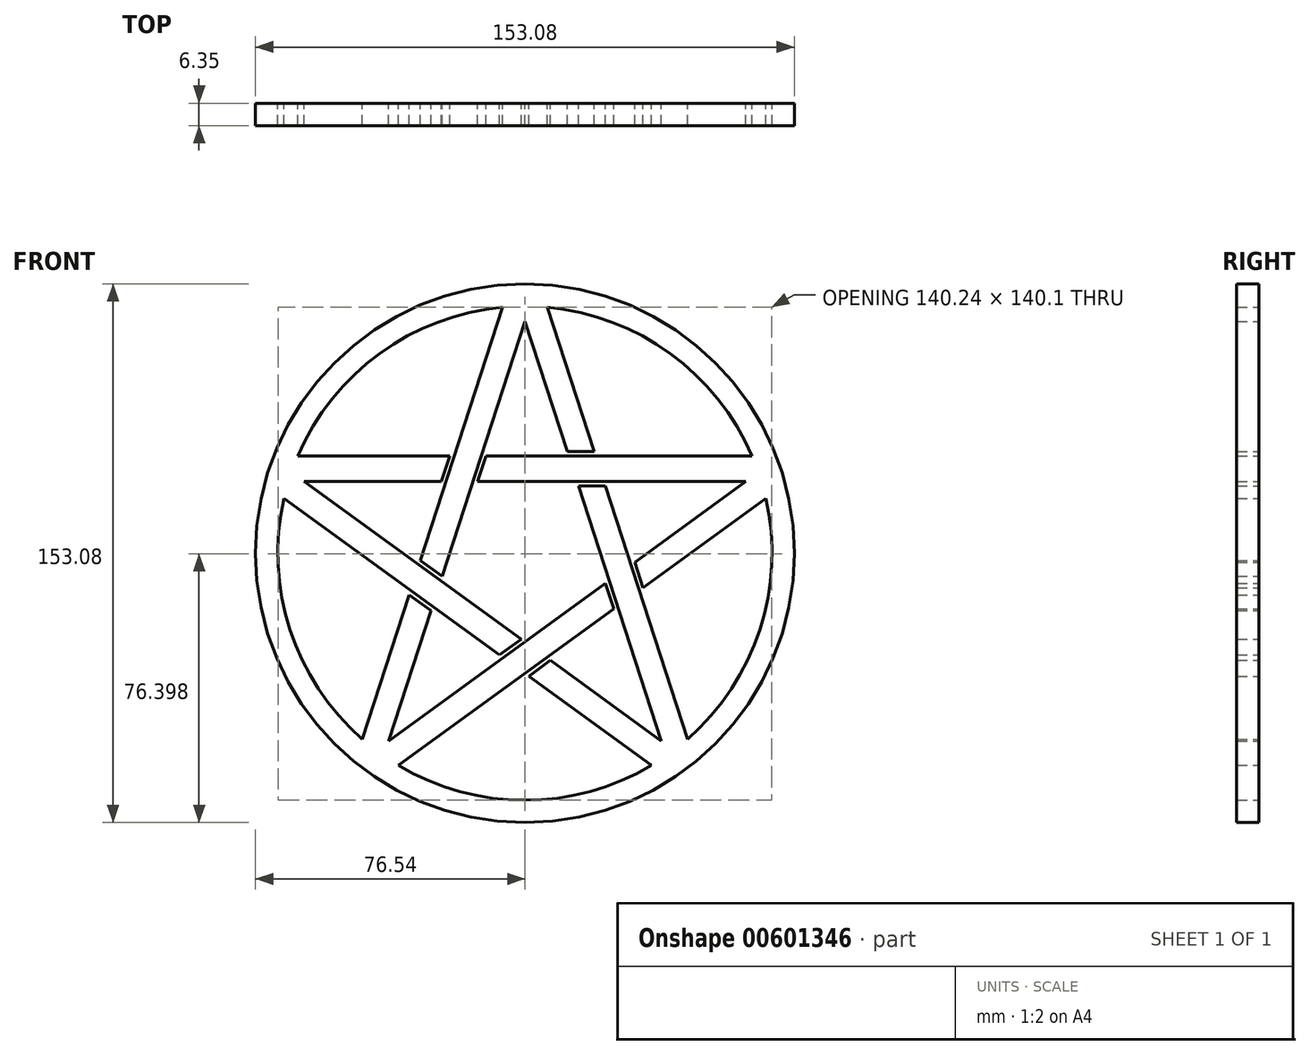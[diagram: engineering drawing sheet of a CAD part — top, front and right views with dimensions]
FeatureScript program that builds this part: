
annotation { "Feature Type Name" : "Feature", "Feature Type Description" : "" }
export const myFeature = defineFeature(function(context is Context, id is Id, definition is map)
    precondition{}
    {
        {
            var Q0;
            Q0=qCreatedBy(makeId("Front.planeOp"),FACE);
            var sketch = newSketch(context, id + "F0", { "sketchPlane" : qUnion([Q0])});
            skCircle(sketch, "E0", {"center": v(0, 0) * mm, "radius": 76.54 * mm});
            skArc(sketch, "E1.0", {"start": v(-6.3, 69.9) * mm, "mid": v(-41.26, 56.79) * mm, "end": v(-64.54, 27.6) * mm});
            skLineSegment(sketch, "E2.0", {"start": v(-38.75, -53.33) * mm, "end": v(-26.71, -16.28) * mm});
            skLineSegment(sketch, "E3.0", {"start": v(-46.2, -52.85) * mm, "end": v(-32.86, -11.81) * mm});
            skLineSegment(sketch, "E4.1.0", {"start": v(38.75, -53.33) * mm, "end": v(7.23, -30.43) * mm});
            skLineSegment(sketch, "E4.1.1", {"start": v(35.99, -60.26) * mm, "end": v(1.08, -34.9) * mm});
            skLineSegment(sketch, "E4.2.1", {"start": v(68.43, 15.6) * mm, "end": v(33.53, -9.76) * mm});
            skLineSegment(sketch, "E4.3.0", {"start": v(0, 65.93) * mm, "end": v(12.04, 28.87) * mm});
            skLineSegment(sketch, "E4.3.1", {"start": v(6.3, 69.9) * mm, "end": v(19.64, 28.87) * mm});
            skLineSegment(sketch, "E4.4.0", {"start": v(-62.7, 20.37) * mm, "end": v(-23.74, 20.37) * mm});
            skLineSegment(sketch, "E4.4.1", {"start": v(-64.54, 27.6) * mm, "end": v(-21.39, 27.6) * mm});
            skPoint(sketch, "E5.orphan", {"position": v(-3.86, 77.45) * mm});
            skPoint(sketch, "E6.orphan", {"position": v(3.86, 77.45) * mm});
            skPoint(sketch, "E7.orphan", {"position": v(-3.02, 75.22) * mm});
            skPoint(sketch, "E8.orphan", {"position": v(0, 76.54) * mm});
            skPoint(sketch, "E9.orphan", {"position": v(48.64, -60.4) * mm});
            skPoint(sketch, "E10.orphan", {"position": v(42.4, -64.93) * mm});
            skPoint(sketch, "E11.orphan", {"position": v(46.66, -59.08) * mm});
            skPoint(sketch, "E12.orphan", {"position": v(41.77, -62.63) * mm});
            skArc(sketch, "E13.trimOffspring", {"start": v(46.2, -52.85) * mm, "mid": v(66.76, -21.7) * mm, "end": v(68.43, 15.6) * mm});
            skPoint(sketch, "E14.orphan", {"position": v(-72.47, 27.6) * mm});
            skPoint(sketch, "E15.orphan", {"position": v(-74.85, 20.27) * mm});
            skPoint(sketch, "E16.orphan", {"position": v(-70.6, 26.12) * mm});
            skPoint(sketch, "E17.orphan", {"position": v(-72.47, 20.37) * mm});
            skArc(sketch, "E18.trimOffspring", {"start": v(-68.43, 15.6) * mm, "mid": v(-66.76, -21.7) * mm, "end": v(-46.2, -52.85) * mm});
            skPoint(sketch, "E19.orphan", {"position": v(72.47, 27.6) * mm});
            skPoint(sketch, "E20.orphan", {"position": v(74.85, 20.27) * mm});
            skPoint(sketch, "E21.orphan", {"position": v(72.47, 20.37) * mm});
            skLineSegment(sketch, "E22.trimOffspring", {"start": v(62.7, 20.37) * mm, "end": v(31.18, -2.53) * mm});
            skArc(sketch, "E23.trimOffspring", {"start": v(64.54, 27.6) * mm, "mid": v(41.26, 56.79) * mm, "end": v(6.3, 69.9) * mm});
            skPoint(sketch, "E24.orphan", {"position": v(-48.64, -60.4) * mm});
            skPoint(sketch, "E25.orphan", {"position": v(-42.4, -64.93) * mm});
            skPoint(sketch, "E26.orphan", {"position": v(-41.77, -62.63) * mm});
            skPoint(sketch, "E27.orphan", {"position": v(-46.66, -59.08) * mm});
            skArc(sketch, "E28.trimOffspring", {"start": v(-35.99, -60.26) * mm, "mid": v(0, -70.2) * mm, "end": v(35.99, -60.26) * mm});
            skLineSegment(sketch, "E29", {"start": v(-21.39, 27.6) * mm, "end": v(-23.74, 20.37) * mm});
            skLineSegment(sketch, "E30.trimOffspring", {"start": v(-13.47, 20.37) * mm, "end": v(62.7, 20.37) * mm});
            skLineSegment(sketch, "E31.trimOffspring", {"start": v(-11.12, 27.6) * mm, "end": v(64.54, 27.6) * mm});
            skLineSegment(sketch, "E32", {"start": v(-11.12, 27.6) * mm, "end": v(-13.47, 20.37) * mm});
            skLineSegment(sketch, "E33.trimOffspring", {"start": v(15.21, 19.1) * mm, "end": v(38.75, -53.33) * mm});
            skLineSegment(sketch, "E34.trimOffspring", {"start": v(22.82, 19.1) * mm, "end": v(46.2, -52.85) * mm});
            skLineSegment(sketch, "E35", {"start": v(31.18, -2.53) * mm, "end": v(33.53, -9.76) * mm});
            skLineSegment(sketch, "E36.trimOffspring", {"start": v(22.87, -8.57) * mm, "end": v(-38.75, -53.33) * mm});
            skLineSegment(sketch, "E37.trimOffspring", {"start": v(25.22, -15.8) * mm, "end": v(-35.99, -60.26) * mm});
            skLineSegment(sketch, "E38", {"start": v(22.87, -8.57) * mm, "end": v(25.22, -15.8) * mm});
            skLineSegment(sketch, "E39.trimOffspring", {"start": v(-1.08, -24.4) * mm, "end": v(-62.7, 20.37) * mm});
            skLineSegment(sketch, "E40.trimOffspring", {"start": v(-7.23, -28.86) * mm, "end": v(-68.43, 15.6) * mm});
            skLineSegment(sketch, "E41", {"start": v(-32.86, -11.81) * mm, "end": v(-26.71, -16.28) * mm});
            skLineSegment(sketch, "E42", {"start": v(-29.69, -2.04) * mm, "end": v(-23.54, -6.51) * mm});
            skLineSegment(sketch, "E43.trimOffspring", {"start": v(-29.69, -2.04) * mm, "end": v(-6.3, 69.9) * mm});
            skLineSegment(sketch, "E44.trimOffspring", {"start": v(-23.54, -6.51) * mm, "end": v(0, 65.93) * mm});
            skLineSegment(sketch, "E45", {"start": v(12.04, 28.87) * mm, "end": v(19.64, 28.87) * mm});
            skLineSegment(sketch, "E46", {"start": v(15.21, 19.1) * mm, "end": v(22.82, 19.1) * mm});
            skLineSegment(sketch, "E47", {"start": v(7.23, -30.43) * mm, "end": v(1.08, -34.9) * mm});
            skLineSegment(sketch, "E48", {"start": v(-1.08, -24.4) * mm, "end": v(-7.23, -28.86) * mm});
            skSolve(sketch);
        }
        {
            var Q0;
            Q0=makeQuery(id+"F0.imprint","IMPRINT",FACE,{"disambiguationData":[TD([[makeQuery(id+"F0.imprint","IMPRINT",EDGE,{"derivedFrom":sQuery(id+"F0.wireOp",EDGE,"E0")}),1.0]])]});
            extrude(context, id + "F1", {"entities" : qUnion([Q0]), "depth" : 6.35 * mm, "offsetDistance" : 25.4 * mm});
        }
    });
